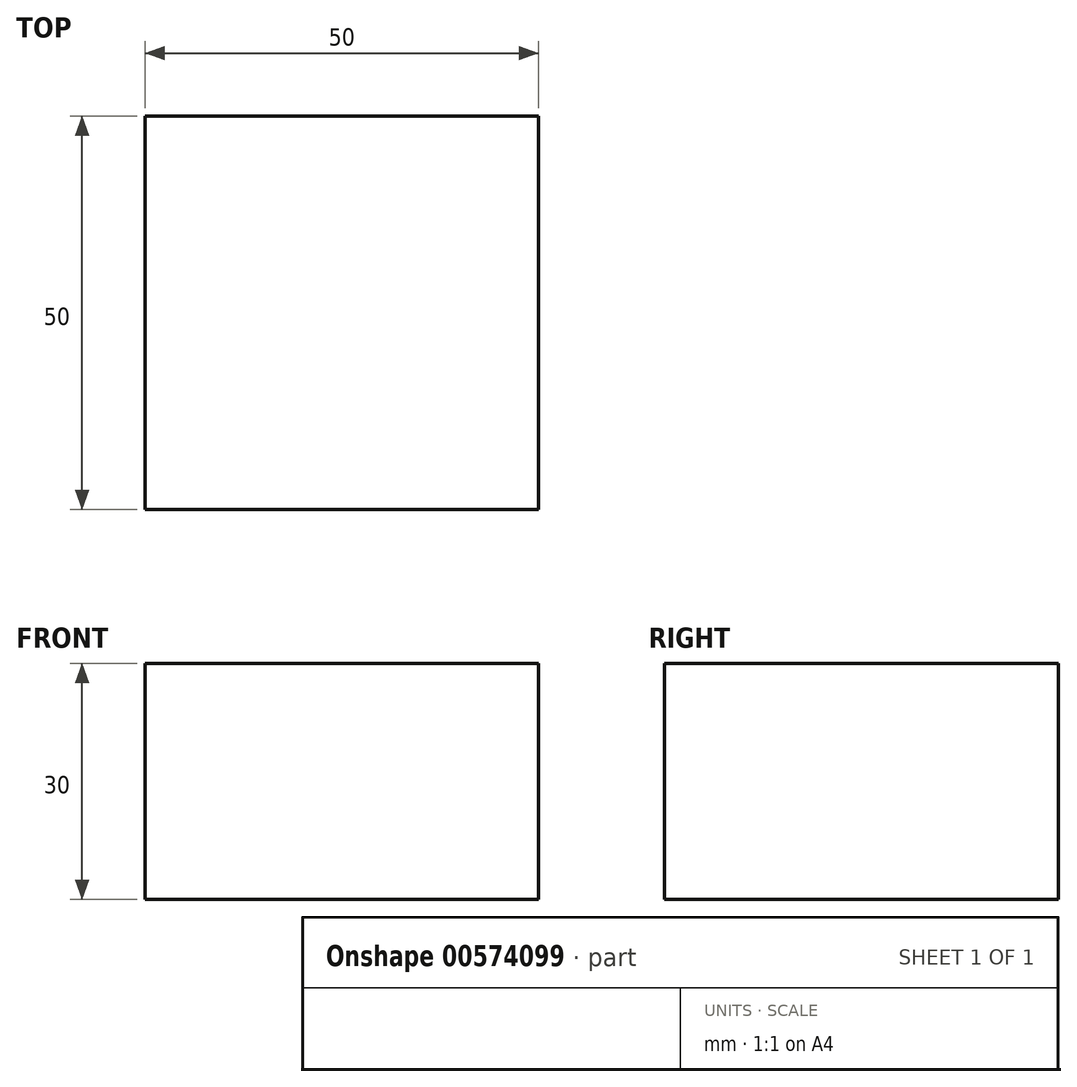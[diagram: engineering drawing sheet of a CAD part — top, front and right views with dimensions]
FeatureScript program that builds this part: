
annotation { "Feature Type Name" : "Feature", "Feature Type Description" : "" }
export const myFeature = defineFeature(function(context is Context, id is Id, definition is map)
    precondition{}
    {
        {
            var Q0;
            Q0=qCreatedBy(makeId("Top.planeOp"),FACE);
            var sketch = newSketch(context, id + "F0", { "sketchPlane" : qUnion([Q0])});
            skLineSegment(sketch, "E0", {"start": v(-25, 25) * mm, "end": v(25, 25) * mm});
            skLineSegment(sketch, "E1", {"start": v(25, 25) * mm, "end": v(25, -25) * mm});
            skLineSegment(sketch, "E2", {"start": v(25, -25) * mm, "end": v(-25, -25) * mm});
            skLineSegment(sketch, "E3", {"start": v(-25, -25) * mm, "end": v(-25, 25) * mm});
            skSolve(sketch);
        }
        {
            var Q0;
            Q0 = qSketchRegion(id + "F0", true);
            extrude(context, id + "F1", {"entities" : qUnion([Q0]), "depth" : 30 * mm, "offsetDistance" : 25 * mm});
        }
    });
